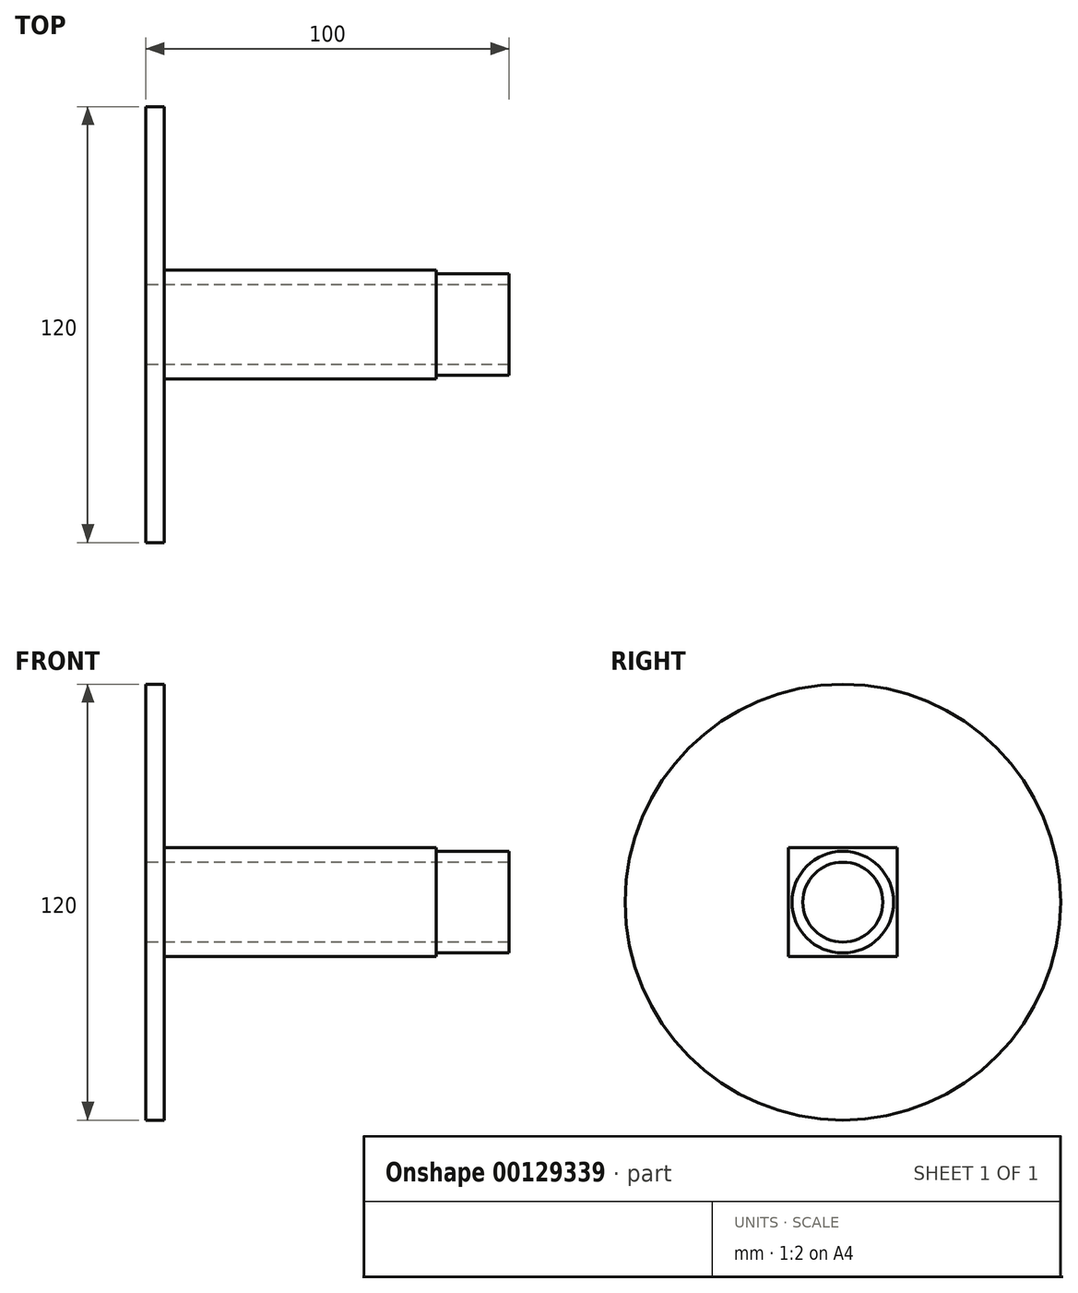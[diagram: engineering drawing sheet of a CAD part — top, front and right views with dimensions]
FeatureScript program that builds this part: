
annotation { "Feature Type Name" : "Feature", "Feature Type Description" : "" }
export const myFeature = defineFeature(function(context is Context, id is Id, definition is map)
    precondition{}
    {
        {
            var Q0;
            Q0=qCreatedBy(makeId("Right.planeOp"),FACE);
            var sketch = newSketch(context, id + "F0", { "sketchPlane" : qUnion([Q0])});
            skCircle(sketch, "E0", {"center": v(0, 0) * mm, "radius": 60 * mm});
            skCircle(sketch, "E1", {"center": v(0, 0) * mm, "radius": 11 * mm});
            skLineSegment(sketch, "E2.bottom", {"start": v(15, -15) * mm, "end": v(-15, -15) * mm});
            skLineSegment(sketch, "E2.top", {"start": v(15, 15) * mm, "end": v(-15, 15) * mm});
            skLineSegment(sketch, "E2.left", {"start": v(15, -15) * mm, "end": v(15, 15) * mm});
            skLineSegment(sketch, "E2.right", {"start": v(-15, -15) * mm, "end": v(-15, 15) * mm});
            skCircle(sketch, "E3", {"center": v(0, 0) * mm, "radius": 14 * mm});
            skSolve(sketch);
        }
        {
            var Q0;
            Q0=makeQuery(id+"F0.imprint","IMPRINT",FACE,{"disambiguationData":[TD([[makeQuery(id+"F0.imprint","IMPRINT",EDGE,{"derivedFrom":sQuery(id+"F0.wireOp",EDGE,"E1")}),-1.0]])]});
            extrude(context, id + "F1", {"entities" : qUnion([Q0]), "depth" : 100 * mm});
        }
        {
            var Q0;
            Q0=makeQuery(id+"F0.imprint","IMPRINT",FACE,{"disambiguationData":[TD([[makeQuery(id+"F0.imprint","IMPRINT",EDGE,{"derivedFrom":sQuery(id+"F0.wireOp",EDGE,"E2.bottom")}),-1.0]])]});
            extrude(context, id + "F2", {"entities" : qUnion([Q0]), "operationType" : NewBodyOperationType.ADD, "depth" : 80 * mm});
        }
        {
            var Q0;
            Q0=makeQuery(id+"F0.imprint","IMPRINT",FACE,{"disambiguationData":[TD([[makeQuery(id+"F0.imprint","IMPRINT",EDGE,{"derivedFrom":sQuery(id+"F0.wireOp",EDGE,"E0")}),1.0]])]});
            extrude(context, id + "F3", {"entities" : qUnion([Q0]), "operationType" : NewBodyOperationType.ADD, "depth" : 5 * mm});
        }
    });
